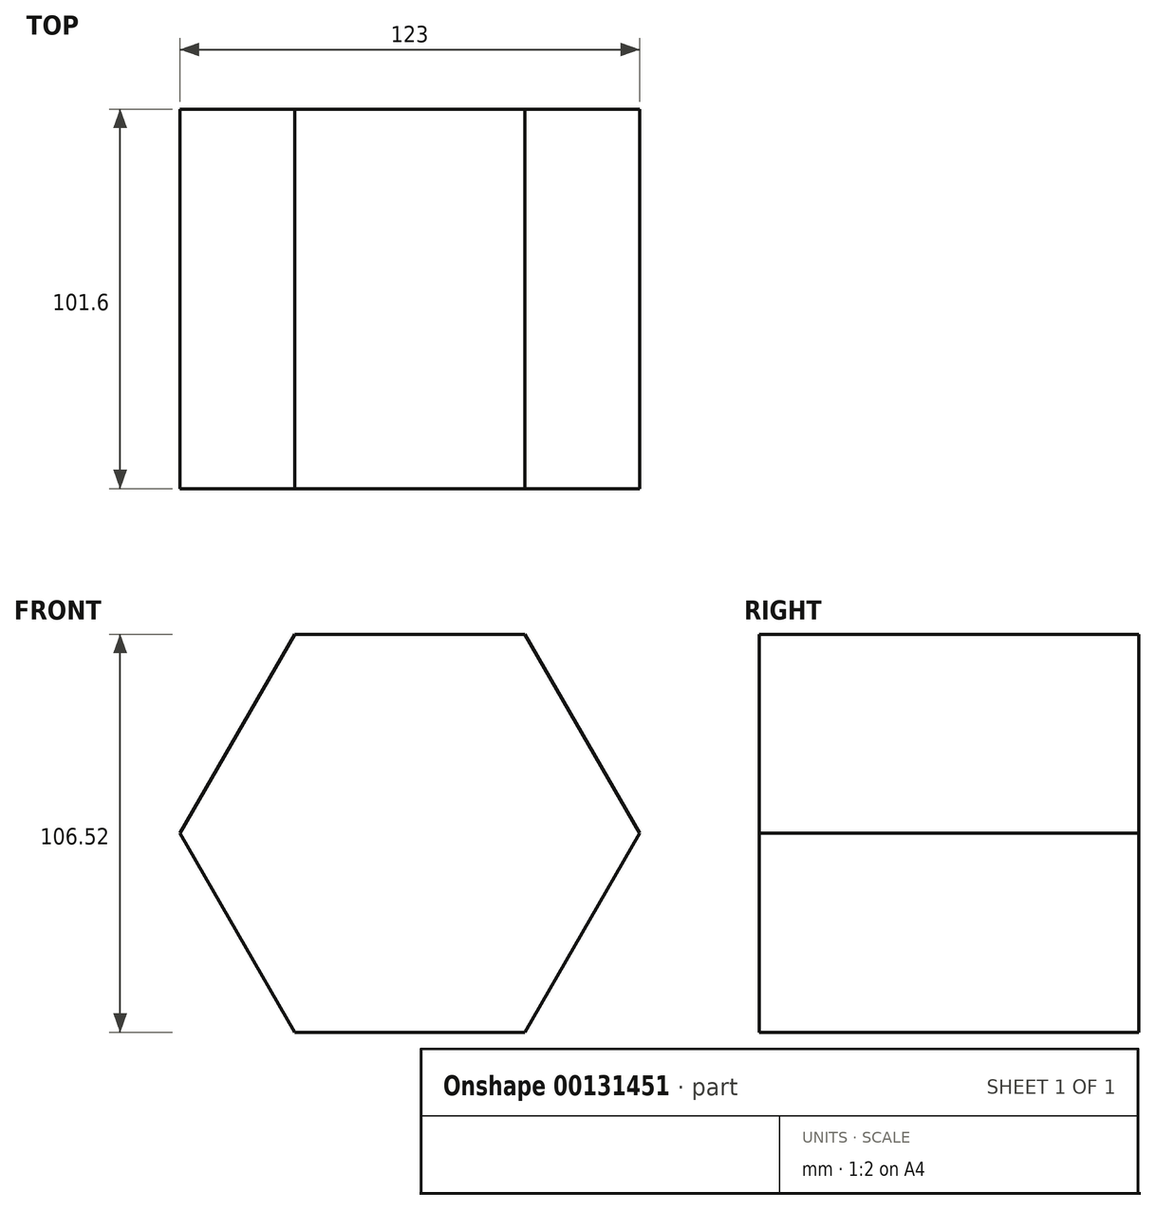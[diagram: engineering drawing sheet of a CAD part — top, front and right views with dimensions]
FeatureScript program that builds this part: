
annotation { "Feature Type Name" : "Feature", "Feature Type Description" : "" }
export const myFeature = defineFeature(function(context is Context, id is Id, definition is map)
    precondition{}
    {
        {
            var Q0;
            Q0=qCreatedBy(makeId("Front.planeOp"),FACE);
            var sketch = newSketch(context, id + "F0", { "sketchPlane" : qUnion([Q0])});
            skCircle(sketch, "E0.cCircle", {"center": v(0, 0) * mm, "radius": 61.5 * mm, "construction": true});
            skLineSegment(sketch, "E0.0", {"start": v(-61.5, 0) * mm, "end": v(-30.75, 53.26) * mm});
            skLineSegment(sketch, "E0.1", {"start": v(-30.75, 53.26) * mm, "end": v(30.75, 53.26) * mm});
            skLineSegment(sketch, "E0.2", {"start": v(30.75, 53.26) * mm, "end": v(61.5, 0) * mm});
            skLineSegment(sketch, "E0.3", {"start": v(61.5, 0) * mm, "end": v(30.75, -53.26) * mm});
            skLineSegment(sketch, "E0.4", {"start": v(30.75, -53.26) * mm, "end": v(-30.75, -53.26) * mm});
            skLineSegment(sketch, "E0.5", {"start": v(-30.75, -53.26) * mm, "end": v(-61.5, 0) * mm});
            skSolve(sketch);
        }
        {
            var Q0;
            Q0=makeQuery(id+"F0.imprint","IMPRINT",FACE,{"disambiguationData":[TD([[makeQuery(id+"F0.imprint","IMPRINT",EDGE,{"derivedFrom":sQuery(id+"F0.wireOp",EDGE,"E0.0")}),-1.0]])]});
            extrude(context, id + "F1", {"entities" : qUnion([Q0]), "depth" : 101.6 * mm});
        }
    });
